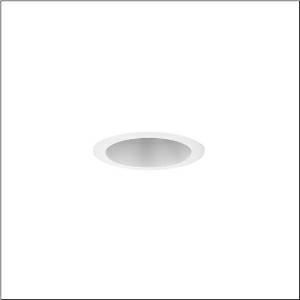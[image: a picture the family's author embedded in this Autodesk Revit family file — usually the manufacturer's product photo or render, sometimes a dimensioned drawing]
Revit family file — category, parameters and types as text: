
# Revit family: lunis_31_mini_51dn167e41
name_source: partatom
category: Lighting Fixtures
units: mm (PartAtom-declared; Revit-internal decimal feet)

## family parameters
Cut with Voids When Loaded = No
Host = Face
Light Source = No
Part Type = Normal
Room Calculation Point = No
Round Connector Dimension = Use Diameter
Shared = No

## types (1)
- Lunis 31 mini (1 x LED, 1040 lm, 8.3 W, 4000K)
    Apparent Load = 8 VA
    CIE Flux Codes = 69 93 99 100 100
    Color Rendering = 80
    Color Temperature = 4000K
    Default Elevation = 1800 mm
    Description = Lunis 31,  mini, downlight, light control with reflector, light emission: direct distribution, LED rated luminous flux: 1.040lm, light colour: 840, control gear: ECG, mains connection: 220..240V, AC, 50/60Hz, housing, white, protection rating (complete): IP20, insulation class (complete): insulation class II (safety insulation), certification: CE, packaging unit: 1 piece
    Height = 0 mm  [stored 0 ft]
    Lamp = 1 x LED
    Lamp Light Flux = 1040 lm
    Lamp Power = 8.3 W
    Lamp count = 1
    Length = 188 mm  [stored 0.616798 ft]
    Luminous efficacy = 125 lm/W
    Manufacturer = Siteco
    ModVariant = No
    Model = 51DN167E41
    Mounting Place = Ceiling
    Mounting Type = Recessed
    Number of Poles = 1
    OnlyDefault = Yes
    Power Factor = 1
    Product Name = Lunis 31 mini
    Product group = downlight | ceiling recessed
    ProductGroupID = 402
    Protection Class = Protection class II
    Protection Degree = IP 20
    RLX_Detail_Level = 1
    RlxData = <blob elided: 21805 chars, md5=eb8c6613>
    Socket = socket
    Standby Power = 0 W
    System Light Flux = 1040 lm
    System Power = 8 W
    Type Comments = Product without accessories
    Type Image = l_1005624.jpg
    URL = http://relux.com
    VarID = ---
    Voltage = 0 V
    Weight = 0.00 kg
    Width = 0 mm  [stored 0 ft]

note: [stored X ft] marks values corroborated as IEEE doubles in the binary element streams (Revit-internal decimal feet)

## geometry (parser evidence)
native form markers: Blend x4, Sweep x11
no freeform markers — native parametric forms only
